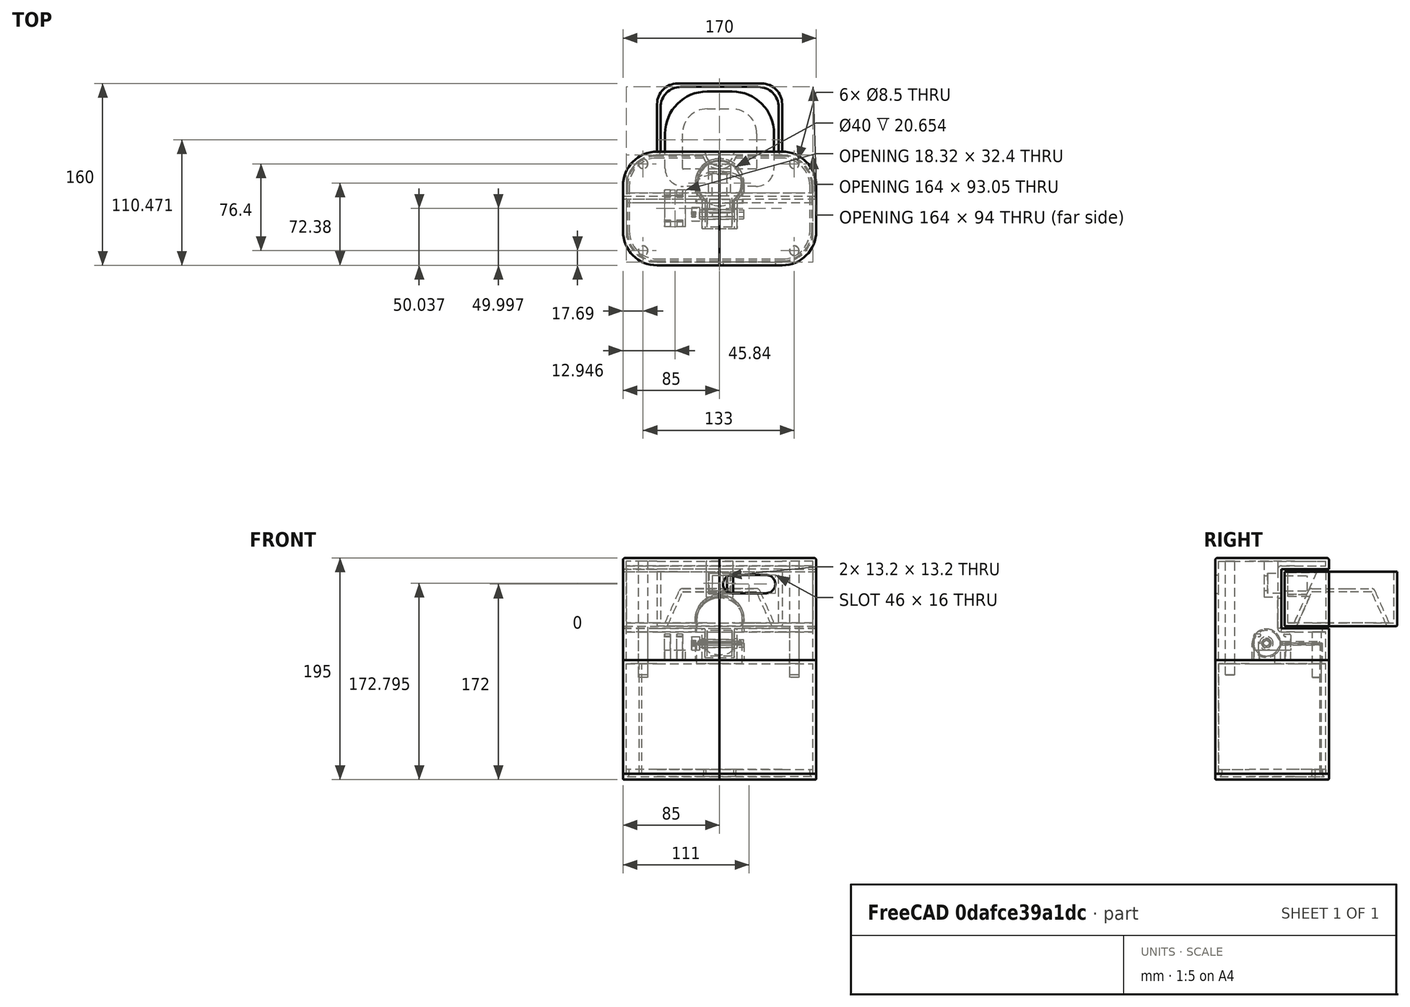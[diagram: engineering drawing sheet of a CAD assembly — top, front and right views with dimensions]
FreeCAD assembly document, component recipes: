
FREECAD ASSEMBLY — COMPONENT RECIPES ("Feeder V3")

This assembly document has 6 components, labeled P0..P5 below (a component is one placed body or linked part). 6 of them carry a construction recipe — the FreeCAD feature program that regenerates the part from scratch, quoted from this document or its linked companion documents; the rest are supplied as boundary geometry only. No exploded tour is included for this assembly.
COMPONENT P0 — recipe-attached ("Body001_CutLink", modeled in this document).
Construction recipe (the document's own serialized feature program — sketch geometry with constraints, then the solid features built on it; lengths are millimeters unless a unit is written):

FEATURE [PartDesign::Plane] CopyDatumPlane
  Length = 62.6838
  Placement = pos=(-2.6041e-12,-27.4425,215) rot=(0.707107,0.707107,0;3.14159rad)
  ResizeMode = 0
  Width = 60.2413
FEATURE [PartDesign::SubShapeBinder] Binder
  BindCopyOnChange = 0
  BindMode = 0
  ClaimChildren = false
  Context = -> Body001 [Binder.]
  Fuse = false
  MakeFace = true
  OffsetFill = false
  OffsetIntersection = false
  OffsetJoinType = 0
  OffsetOpenResult = false
  PartialLoad = false
  Refine = true
  Relative = true
  Support = -> [Body[Pocket004.Edge74,Pocket004.Face29,Pocket004.Face33,Pocket004.Edge73]]
  _Version = 2
FEATURE [Sketcher::SketchObject] Sketch011
  ArcFitTolerance = 1e-06
  AttachmentSupport = -> [Binder]
  ExternalGeometry = -> [Binder]
  FullyConstrained = true
  MakeInternals = false
  MapMode = 5
  Placement = pos=(-13,0,0) rot=(0.57735,0.57735,0.57735;2.0944rad)
  sketch-geometry (7):
    g0: LineSegment StartX=-31.6637 StartY=215 StartZ=0 EndX=-29.5387 EndY=211.319 EndZ=0
    g1: LineSegment StartX=-29.5387 StartY=211.319 StartZ=0 EndX=-25.2887 EndY=211.319 EndZ=0
    g2: LineSegment StartX=-25.2887 StartY=211.319 StartZ=0 EndX=-23.1637 EndY=215 EndZ=0
    g3: LineSegment StartX=-23.1637 StartY=215 StartZ=0 EndX=-25.2887 EndY=218.681 EndZ=0
    g4: LineSegment StartX=-25.2887 StartY=218.681 StartZ=0 EndX=-29.5387 EndY=218.681 EndZ=0
    g5: LineSegment StartX=-29.5387 StartY=218.681 StartZ=0 EndX=-31.6637 EndY=215 EndZ=0
    g6: Circle [constr] CenterX=-27.4137 CenterY=215 CenterZ=0 NormalX=0 NormalY=0 NormalZ=1 AngleXU=0 Radius=4.25
  constraints (19):
    c: Coincident(g0,g1)
    c: Coincident(g1,g2)
    c: Coincident(g2,g3)
    c: Coincident(g3,g4)
    c: Coincident(g4,g5)
    c: Coincident(g5,g0)
    c: Equal(g0, g1-g5) x5
    c: PointOnObject(g0,g6)
    c: PointOnObject(g1,g6)
    c: PointOnObject(g2,g6)
    c: PointOnObject(g3,g6)
    c: PointOnObject(g4,g6)
    c: PointOnObject(g5,g6)
    c: Coincident(g6,g-5)
    c: PointOnObject(g5,g-4)
    c: Horizontal(g2,g6)
    c: DistanceX(g-5,g-6) = 59.9137
    c: DistanceX(g-6,g-6) = 34.9137
    c: DistanceX(g-5,g-6) = 25
FEATURE [Sketcher::SketchObject] Sketch012
  ArcFitTolerance = 1e-06
  AttachmentSupport = -> [YZ_Plane001]
  ExternalGeometry = -> [Binder]
  FullyConstrained = true
  MakeInternals = false
  MapMode = 5
  Placement = pos=(0,0,0) rot=(0.57735,0.57735,0.57735;2.0944rad)
  sketch-geometry (7):
    g0: ArcOfCircle CenterX=-27.4137 CenterY=215 CenterZ=0 NormalX=0 NormalY=0 NormalZ=1 AngleXU=0 Radius=11.25 StartAngle=3.14159 EndAngle=5.83678
    g1: LineSegment StartX=-15.66 StartY=213.499 StartZ=0 EndX=-17.2662 EndY=210.143 EndZ=0
    g2: ArcOfCircle CenterX=-27.4137 CenterY=215 CenterZ=0 NormalX=0 NormalY=0 NormalZ=1 AngleXU=0 Radius=11.25 StartAngle=0.444057 EndAngle=3.14159
    g3: LineSegment StartX=-15.6685 StartY=216.499 StartZ=0 EndX=-17.2548 EndY=219.833 EndZ=0
    g4: LineSegment StartX=-15.6685 StartY=216.499 StartZ=0 EndX=0 EndY=216.499 EndZ=0
    g5: LineSegment StartX=0 StartY=216.499 StartZ=0 EndX=0 EndY=213.499 EndZ=0
    g6: LineSegment StartX=-15.66 StartY=213.499 StartZ=0 EndX=0 EndY=213.499 EndZ=0
  constraints (18):
    c: Horizontal(g0,g0)
    c: Tangent(g0,g1) = 1.5708
    c: Coincident(g0,g-4)
    c: Tangent(g2,g3) = -1.5708
    c: Radius(g2) = 11.25
    c: Horizontal(g4)
    c: Coincident(g3,g4)
    c: Coincident(g0,g2)
    c: DistanceY(g0,g2) = 9.69
    c: Coincident(g5,g4)
    c: Vertical(g5)
    c: Coincident(g0,g2)
    c: PointOnObject(g4,g-2)
    c: Block(g5)
    c: DistanceX(g1,g5) = 15.66
    c: Coincident(g6,g1)
    c: Coincident(g6,g5)
    c: Horizontal(g6)
FEATURE [PartDesign::Pad] Pad019  label="Door Pin width"
  Direction = (1,0,0)
  Length = 22
  Length2 = 10
  Midplane = true
  Placement = pos=(0,0,0) rot=(1,1,1;2.0944rad)
  Profile = -> Sketch012
  ReferenceAxis = -> Sketch012 [N_Axis]
  Refine = true
  Suppressed = false
  Type = 0
FEATURE [Sketcher::SketchObject] Sketch015
  ArcFitTolerance = 1e-06
  AttachmentSupport = -> [Pad019]
  FullyConstrained = true
  MakeInternals = false
  MapMode = 5
  Placement = pos=(0,4.76e-14,216.499) rot=(0,0,-1;1.5708rad)
  sketch-geometry (5):
    g0: LineSegment StartX=1.545e-13 StartY=-11 StartZ=0 EndX=1.616e-13 EndY=11 EndZ=0
    g1: LineSegment StartX=1.616e-13 StartY=11 StartZ=0 EndX=15.6637 EndY=11 EndZ=0
    g2: LineSegment StartX=1.545e-13 StartY=-11 StartZ=0 EndX=15.6637 EndY=-11 EndZ=0
    g3: LineSegment StartX=15.6637 StartY=11 StartZ=0 EndX=0 EndY=1.8e-15 EndZ=0
    g4: LineSegment StartX=0 StartY=1.8e-15 StartZ=0 EndX=15.6637 EndY=-11 EndZ=0
  constraints (10):
    c: Coincident(g0,g-4)
    c: Coincident(g0,g-6)
    c: Coincident(g1,g0)
    c: Coincident(g1,g-6)
    c: Coincident(g2,g0)
    c: Coincident(g2,g-5)
    c: Coincident(g3,g-6)
    c: Coincident(g3,g-1)
    c: Coincident(g4,g3)
    c: Coincident(g4,g2)
FEATURE [PartDesign::Pocket] Pocket014  label="Door Cut"
  BaseFeature = -> Pad019
  Direction = (0,0,-1)
  Length = 0
  Length2 = 5
  Placement = pos=(0,0,0) rot=(1,1,1;2.0944rad)
  Profile = -> Sketch015
  ReferenceAxis = -> Sketch015 [N_Axis]
  Refine = true
  Suppressed = false
  Type = 3
  UpToFace = -> Pad019 [Face2]
FEATURE [PartDesign::Pocket] Pocket015  label="Door Pin Hole"
  BaseFeature = -> Pocket014
  Direction = (-1,0,0)
  Length = 5
  Length2 = 5
  Placement = pos=(0,0,0) rot=(1,1,1;2.0944rad)
  Profile = -> Sketch011
  ReferenceAxis = -> Sketch011 [N_Axis]
  Refine = true
  Reversed = true
  Suppressed = false
  Type = 1
FEATURE [PartDesign::Revolution] Revolution
  Angle = 360
  Angle2 = 60
  Axis = (7e-16,-2e-16,-1)
  Base = (-1.665e-13,1.202e-13,216.499)
  BaseFeature = -> Pocket015
  Placement = pos=(0,0,0) rot=(1,1,1;2.0944rad)
  Profile = -> Pocket015 [Face8]
  ReferenceAxis = -> Pocket015 [Edge37]
  Refine = true
  Suppressed = false
  Type = 3
  UpToFace = -> Pocket015 [Face9]
FEATURE [PartDesign::Fillet] Fillet001
  Base = -> Revolution [Edge32,Edge1]
  BaseFeature = -> Revolution
  Placement = pos=(0,0,0) rot=(1,1,1;2.0944rad)
  Radius = 4
  Refine = true
  SupportTransform = false
  Suppressed = false
  UseAllEdges = false
FEATURE [PartDesign::Body] Body001  label="Storage Door"
  AllowCompound = false
  Group = -> [CopyDatumPlane,Binder,Sketch011,Sketch012,Sketch015,Pad019,Pocket014,Pocket015,Revolution,Fillet001]
  Origin = -> Origin001
  Tip = -> Fillet001
COMPONENT P1 — recipe-attached ("Body002_CutLink", modeled in this document).
Construction recipe (the document's own serialized feature program — sketch geometry with constraints, then the solid features built on it; lengths are millimeters unless a unit is written):

FEATURE [PartDesign::SubShapeBinder] Binder001
  BindCopyOnChange = 0
  BindMode = 0
  ClaimChildren = false
  Context = -> Body002 [Binder001.]
  Fuse = false
  MakeFace = true
  OffsetFill = false
  OffsetIntersection = false
  OffsetJoinType = 0
  OffsetOpenResult = false
  PartialLoad = false
  Refine = true
  Relative = true
  Support = -> [Body[Pocket004.Face23,Pocket004.Face21]]
  _Version = 2
FEATURE [PartDesign::SubShapeBinder] Binder002
  BindCopyOnChange = 0
  BindMode = 0
  ClaimChildren = false
  Context = -> Body002 [Binder002.]
  Fuse = false
  MakeFace = true
  OffsetFill = false
  OffsetIntersection = false
  OffsetJoinType = 0
  OffsetOpenResult = false
  PartialLoad = false
  Refine = true
  Relative = true
  Support = -> [Body001[Pocket006.Face3]]
  _Version = 2
FEATURE [PartDesign::Plane] CopyDatumPlane001
  Length = 74.8801
  Placement = pos=(0,-27.4425,215) rot=(0.57735,0.57735,0.57735;2.0944rad)
  ResizeMode = 0
  Width = 262.438
FEATURE [Sketcher::SketchObject] Sketch016
  ArcFitTolerance = 1e-06
  AttachmentSupport = -> [CopyDatumPlane001]
  ExternalGeometry = -> [Binder002]
  FullyConstrained = true
  MakeInternals = false
  MapMode = 5
  Placement = pos=(0,-27.4425,215) rot=(0.57735,0.57735,0.57735;2.0944rad)
  sketch-geometry (7):
    g0: LineSegment StartX=3.9 StartY=0 StartZ=0 EndX=1.95 EndY=3.3775 EndZ=0
    g1: LineSegment StartX=1.95 StartY=3.3775 StartZ=0 EndX=-1.95 EndY=3.3775 EndZ=0
    g2: LineSegment StartX=-1.95 StartY=3.3775 StartZ=0 EndX=-3.9 EndY=4.765e-13 EndZ=0
    g3: LineSegment StartX=-3.9 StartY=4.765e-13 StartZ=0 EndX=-1.95 EndY=-3.3775 EndZ=0
    g4: LineSegment StartX=-1.95 StartY=-3.3775 StartZ=0 EndX=1.95 EndY=-3.3775 EndZ=0
    g5: LineSegment StartX=1.95 StartY=-3.3775 StartZ=0 EndX=3.9 EndY=0 EndZ=0
    g6: Circle [constr] CenterX=0 CenterY=0 CenterZ=0 NormalX=0 NormalY=0 NormalZ=1 AngleXU=0 Radius=3.9
  constraints (16):
    c: Coincident(g0,g1)
    c: Coincident(g1,g2)
    c: Coincident(g2,g3)
    c: Coincident(g3,g4)
    c: Coincident(g4,g5)
    c: Coincident(g5,g0)
    c: Equal(g0, g1-g5) x5
    c: PointOnObject(g0,g6)
    c: PointOnObject(g1,g6)
    c: PointOnObject(g2,g6)
    c: PointOnObject(g3,g6)
    c: PointOnObject(g4,g6)
    c: PointOnObject(g5,g6)
    c: Radius(g6) = 3.9
    c: Coincident(g6,g-1)
    c: PointOnObject(g5,g-1)
FEATURE [PartDesign::Pad] Pad005  label="Square Push"
  Direction = (1,0,0)
  Length = 42
  Length2 = 10
  Midplane = true
  Placement = pos=(0,-27.4425,215) rot=(0.57735,0.57735,0.57735;2.0944rad)
  Profile = -> Sketch016
  ReferenceAxis = -> Sketch016 [N_Axis]
  Refine = true
  Suppressed = false
  Type = 0
FEATURE [Sketcher::SketchObject] Sketch017
  ArcFitTolerance = 1e-06
  AttachmentSupport = -> [Pad005]
  FullyConstrained = true
  MakeInternals = false
  MapMode = 5
  Placement = pos=(-21,-27.4425,215) rot=(0.57735,0.57735,-0.57735;4.18879rad)
  sketch-geometry (1):
    g0: Circle CenterX=0 CenterY=0 CenterZ=0 NormalX=0 NormalY=0 NormalZ=1 AngleXU=0 Radius=5.9
  constraints (2):
    c: Diameter(g0) = 11.8
    c: Coincident(g0,g-1)
FEATURE [PartDesign::Pad] Pad006  label="Circle push"
  BaseFeature = -> Pad005
  Direction = (-1,0,0)
  Length = 7
  Length2 = 10
  Midplane = true
  Placement = pos=(0,-27.4425,215) rot=(0.57735,0.57735,0.57735;2.0944rad)
  Profile = -> Sketch017
  ReferenceAxis = -> Sketch017 [N_Axis]
  Refine = true
  Suppressed = false
  Type = 0
FEATURE [PartDesign::SubShapeBinder] Binder003  label="Axle Binder"
  BindCopyOnChange = 0
  BindMode = 0
  ClaimChildren = false
  Context = -> Body002 [Binder003.]
  Fuse = false
  MakeFace = true
  OffsetFill = false
  OffsetIntersection = false
  OffsetJoinType = 0
  OffsetOpenResult = false
  PartialLoad = false
  Placement = pos=(3.5,-1.07e-14,0) rot=(0,0,1;0rad)
  Refine = true
  Relative = true
  _Version = 2
FEATURE [Sketcher::SketchObject] Sketch018
  ArcFitTolerance = 1e-06
  AttachmentSupport = -> [Pad006]
  ExternalGeometry = -> [Binder003]
  FullyConstrained = true
  MakeInternals = false
  MapMode = 5
  Placement = pos=(-24.5,-27.4425,215) rot=(0.57735,0.57735,-0.57735;4.18879rad)
  sketch-geometry (5):
    g0: LineSegment StartX=0 StartY=0 StartZ=0 EndX=0 EndY=2.375 EndZ=0
    g1: LineSegment StartX=0 StartY=2.375 StartZ=0 EndX=-0.0980568 EndY=2.47306 EndZ=0
    g2: LineSegment StartX=-0.0980568 StartY=2.47306 StartZ=0 EndX=-0.160985 EndY=2.46976 EndZ=0
    g3: LineSegment StartX=-0.160985 StartY=2.46976 StartZ=0 EndX=-0.248255 EndY=2.36199 EndZ=0
    g4: LineSegment StartX=-0.248255 StartY=2.36199 StartZ=0 EndX=0 EndY=0 EndZ=0
  constraints (10):
    c: Coincident(g0,g-1)
    c: Coincident(g0,g-4)
    c: Coincident(g1,g0)
    c: Coincident(g1,g-4)
    c: Coincident(g3,g2)
    c: Coincident(g3,g-5)
    c: Coincident(g4,g3)
    c: Coincident(g4,g0)
    c: Coincident(g2,g-5)
    c: Coincident(g2,g1)
FEATURE [PartDesign::Pocket] Pocket007  label="Axle form"
  BaseFeature = -> Pad006
  Direction = (1,0,0)
  Length = 3.5
  Length2 = 5
  Placement = pos=(0,-27.4425,215) rot=(0.57735,0.57735,0.57735;2.0944rad)
  Profile = -> Sketch018
  ReferenceAxis = -> Sketch018 [N_Axis]
  Refine = true
  Suppressed = false
  Type = 0
FEATURE [PartDesign::PolarPattern] PolarPattern  label="Axle repeat round"
  Angle = 360
  Axis = -> Sketch018 [N_Axis]
  BaseFeature = -> Pocket007
  Mode = 0
  Occurrences = 60
  Offset = 120
  Originals = -> [Pocket007]
  Placement = pos=(0,-27.4425,215) rot=(0.57735,0.57735,0.57735;2.0944rad)
  Refine = true
  Suppressed = false
  TransformMode = 0
FEATURE [PartDesign::Body] Body002  label="Storage Door Pin"
  AllowCompound = false
  Group = -> [Binder001,Binder002,CopyDatumPlane001,Sketch016,Pad005,Sketch017,Pad006,Sketch018,Binder003,Pocket007,PolarPattern]
  Origin = -> Origin002
  Tip = -> PolarPattern
COMPONENT P2 — recipe-attached ("Body006_CutLink", modeled in this document).
Construction recipe (the document's own serialized feature program — sketch geometry with constraints, then the solid features built on it; lengths are millimeters unless a unit is written):

FEATURE [PartDesign::ShapeBinder] ShapeBinder001  label="Base Shape Binder"
  Support = -> [Pocket008]
  TraceSupport = false
FEATURE [PartDesign::Pad] Pad015  label="Height of base"
  Direction = (0,0,1)
  Length = 90
  Length2 = 10
  Profile = -> ShapeBinder001
  Refine = true
  Suppressed = false
  Type = 0
FEATURE [PartDesign::ShapeBinder] CopyPocket009  label="Storage Door Datum"
  Placement = pos=(0,0,215) rot=(0,0,1;0rad)
  TraceSupport = false
FEATURE [PartDesign::Line] DatumLine001  label="Storage Door Center"
  AttacherType = Attacher::AttachEngineLine
  AttachmentSupport = -> [CopyPocket009]
  Length = 20
  MapMode = 19
  Placement = pos=(0,0,215) rot=(0,0,-1;0.736025rad)
  ResizeMode = 0
FEATURE [PartDesign::Point] DatumPoint001  label="Storage Door Axle"
  AttacherType = Attacher::AttachEnginePoint
  AttachmentSupport = -> [Pocket008]
  MapMode = 36
  Placement = pos=(-15.5,-27.4137,215) rot=(0.707107,0.707107,0;3.14159rad)
FEATURE [Sketcher::SketchObject] Sketch034
  ArcFitTolerance = 1e-06
  AttachmentSupport = -> [Pad015]
  ExternalGeometry = -> [DatumPoint001,CopyPocket009,Pad015]
  FullyConstrained = true
  MakeInternals = false
  MapMode = 5
  Placement = pos=(85,0,0) rot=(0.57735,0.57735,0.57735;2.0944rad)
  sketch-geometry (4):
    g0: LineSegment StartX=84.996 StartY=228 StartZ=0 EndX=84.996 EndY=280 EndZ=0
    g1: LineSegment StartX=84.996 StartY=280 StartZ=0 EndX=-14.434 EndY=280 EndZ=0
    g2: LineSegment StartX=-14.434 StartY=280 StartZ=0 EndX=-14.434 EndY=228 EndZ=0
    g3: LineSegment StartX=-14.434 StartY=228 StartZ=0 EndX=84.996 EndY=228 EndZ=0
  constraints (12):
    c: Coincident(g0,g1)
    c: Coincident(g1,g2)
    c: Coincident(g2,g3)
    c: Coincident(g3,g0)
    c: Vertical(g0)
    c: Vertical(g2)
    c: Horizontal(g1)
    c: Horizontal(g3)
    c: DistanceY(g2,g2) = 52
    c: PointOnObject(g-4,g2)
    c: Distance(g-6,g1) = 10
    c: DistanceX(g3,g3) = 99.43
FEATURE [PartDesign::ShapeBinder] CopyPocket010  label="Hinge length"
  Placement = pos=(0,0,215) rot=(0,0,1;0rad)
  TraceSupport = false
FEATURE [PartDesign::Pocket] Pocket009  label="Food Plate Cut"
  BaseFeature = -> Pad015
  Direction = (-1,0,0)
  Length = 0
  Length2 = 5
  Profile = -> Sketch034
  ReferenceAxis = -> Sketch034 [N_Axis]
  Refine = true
  Suppressed = false
  Type = 3
  UpToFace = -> Pad015 [Face3]
FEATURE [PartDesign::Thickness] Thickness001
  Base = -> Pocket009 [Face2]
  BaseFeature = -> Pocket009
  Intersection = false
  Join = 0
  Mode = 0
  Refine = true
  Reversed = true
  SupportTransform = false
  Suppressed = false
  Value = 3
FEATURE [Sketcher::SketchObject] Sketch037
  ArcFitTolerance = 1e-06
  AttachmentSupport = -> [Thickness001]
  ExternalGeometry = -> [CopyPocket009]
  FullyConstrained = true
  MakeInternals = false
  MapMode = 5
  Placement = pos=(0,0,225) rot=(1,0,0;3.14159rad)
  sketch-geometry (6):
    g0: ArcOfCircle CenterX=0 CenterY=0 CenterZ=0 NormalX=0 NormalY=0 NormalZ=1 AngleXU=0 Radius=21.5 StartAngle=3.0286 EndAngle=6.39618
    g1: LineSegment StartX=20 StartY=34.4342 StartZ=0 EndX=20 EndY=14.4342 EndZ=0
    g2: LineSegment StartX=-20 StartY=34.4342 StartZ=0 EndX=-20 EndY=14.4342 EndZ=0
    g3: ArcOfCircle CenterX=3.5332e-12 CenterY=-35.523 CenterZ=0 NormalX=0 NormalY=0 NormalZ=1 AngleXU=0 Radius=72.76 StartAngle=1.29234 EndAngle=1.84926
    g4: LineSegment StartX=20 StartY=14.4342 StartZ=0 EndX=21.3629 EndY=2.42425 EndZ=0
    g5: LineSegment StartX=-20 StartY=14.4342 StartZ=0 EndX=-21.3629 EndY=2.42425 EndZ=0
  constraints (19):
    c: Coincident(g0,g-1)
    c: Coincident(g3,g2)
    c: Coincident(g1,g3)
    c: DistanceX(g-6,g2) = 3
    c: DistanceX(g1,g-5) = 3
    c: Vertical(g2,g2)
    c: Horizontal(g2,g1)
    c: Radius(g3) = 72.76
    c: Tangent(g0,g5) = -1.5708
    c: Radius(g0) = 21.5
    c: Coincident(g5,g2)
    c: Tangent(g0,g4) = 1.5708
    c: Coincident(g1,g4)
    c: Horizontal(g1,g2)
    c: Vertical(g1)
    c: DistanceY(g5,g5) = 12.01
    c: DistanceY(g4,g4) = 12.01
    c: DistanceY(g1,g1) = 20
    c: DistanceY(g-5,g-5) = 23
FEATURE [PartDesign::Pocket] Pocket010  label="Food door cut"
  BaseFeature = -> Thickness001
  Direction = (0,0,1)
  Length = 0
  Length2 = 5
  Profile = -> Sketch037
  ReferenceAxis = -> Sketch037 [N_Axis]
  Refine = true
  Suppressed = false
  Type = 3
  UpToFace = -> Thickness001 [Face3]
FEATURE [Sketcher::SketchObject] Sketch054
  ArcFitTolerance = 1e-06
  AttachmentSupport = -> [Pocket010]
  ExternalGeometry = -> [Pocket010]
  FullyConstrained = true
  MakeInternals = false
  MapMode = 5
  Placement = pos=(0,-14.434,0) rot=(0,0.707107,0.707107;3.14159rad)
  sketch-geometry (1):
    g0: Circle CenterX=-3.5467e-12 CenterY=233.933 CenterZ=0 NormalX=0 NormalY=0 NormalZ=1 AngleXU=0 Radius=20.8615
  constraints (3):
    c: PointOnObject(g-3,g0)
    c: PointOnObject(g-3,g0)
    c: Block(g0)
FEATURE [PartDesign::Pocket] Pocket024  label="Food door cut001"
  BaseFeature = -> Pocket010
  Direction = (0,-1,2e-16)
  Length = 0
  Length2 = 5
  Profile = -> Sketch054
  ReferenceAxis = -> Sketch054 [N_Axis]
  Refine = true
  Suppressed = false
  Type = 3
  UpToFace = -> Pocket010 [Face32]
FEATURE [Sketcher::SketchObject] Sketch056  label="HX711 Hole"
  ArcFitTolerance = 1e-06
  AttachmentSupport = -> [Pocket024]
  ExternalGeometry = -> [DatumLine001,Pocket024]
  FullyConstrained = true
  MakeInternals = false
  MapMode = 5
  Placement = pos=(0,-14.434,0) rot=(0,0.707107,0.707107;3.14159rad)
  sketch-geometry (10):
    g0: LineSegment StartX=-9 StartY=276.795 StartZ=0 EndX=-9 EndY=258.795 EndZ=0
    g1: LineSegment StartX=-9 StartY=258.795 StartZ=0 EndX=9 EndY=258.795 EndZ=0
    g2: LineSegment StartX=9 StartY=258.795 StartZ=0 EndX=9 EndY=276.795 EndZ=0
    g3: LineSegment StartX=9 StartY=276.795 StartZ=0 EndX=-9 EndY=276.795 EndZ=0
    g4: GeomPoint [constr] X=2.1e-15 Y=267.795 Z=0
    g5: LineSegment StartX=6.6 StartY=261.195 StartZ=0 EndX=6.6 EndY=274.395 EndZ=0
    g6: LineSegment StartX=6.6 StartY=274.395 StartZ=0 EndX=-6.6 EndY=274.395 EndZ=0
    g7: LineSegment StartX=-6.6 StartY=274.395 StartZ=0 EndX=-6.6 EndY=261.195 EndZ=0
    g8: LineSegment StartX=-6.6 StartY=261.195 StartZ=0 EndX=6.6 EndY=261.195 EndZ=0
    g9: GeomPoint [constr] X=2.1e-15 Y=267.795 Z=0
  constraints (25):
    c: Coincident(g0,g1)
    c: Coincident(g1,g2)
    c: Coincident(g2,g3)
    c: Coincident(g3,g0)
    c: Vertical(g0)
    c: Vertical(g2)
    c: Horizontal(g1)
    c: Horizontal(g3)
    c: Symmetric(g2,g0,g4)
    c: PointOnObject(g4,g-3)
    c: DistanceX(g3,g3) = 18
    c: DistanceY(g0,g0) = 18
    c: Distance(g-4,g1) = 4
    c: Coincident(g5,g6)
    c: Coincident(g6,g7)
    c: Coincident(g7,g8)
    c: Coincident(g8,g5)
    c: Vertical(g5)
    c: Vertical(g7)
    c: Horizontal(g6)
    c: Horizontal(g8)
    c: Symmetric(g7,g5,g9)
    c: Coincident(g9,g4)
    c: DistanceX(g8,g8) = 13.2
    c: DistanceY(g7,g7) = 13.2
FEATURE [Sketcher::SketchObject] Sketch057
  ArcFitTolerance = 1e-06
  AttachmentSupport = -> [Pocket024]
  ExternalGeometry = -> [Sketch056,Pocket024]
  FullyConstrained = true
  MakeInternals = false
  MapMode = 5
  Placement = pos=(0,-17.434,0) rot=(1,0,0;1.5708rad)
  sketch-geometry (4):
    g0: LineSegment StartX=-12 StartY=290 StartZ=0 EndX=-12 EndY=255.795 EndZ=0
    g1: LineSegment StartX=-12 StartY=255.795 StartZ=0 EndX=12 EndY=255.795 EndZ=0
    g2: LineSegment StartX=12 StartY=255.795 StartZ=0 EndX=12 EndY=290 EndZ=0
    g3: LineSegment StartX=12 StartY=290 StartZ=0 EndX=-12 EndY=290 EndZ=0
  constraints (11):
    c: Coincident(g0,g1)
    c: Coincident(g1,g2)
    c: Coincident(g2,g3)
    c: Coincident(g3,g0)
    c: Vertical(g0)
    c: Vertical(g2)
    c: Horizontal(g1)
    c: PointOnObject(g0,g-4)
    c: Distance(g1,g-5) = 3
    c: Symmetric(g0,g2,g-2)
    c: Distance(g0,g-6) = 3
FEATURE [PartDesign::Pad] Pad026  label="HX71 Hole width"
  BaseFeature = -> Pocket024
  Direction = (0,-1,2e-16)
  Length = 12
  Length2 = 10
  Profile = -> Sketch057
  ReferenceAxis = -> Sketch057 [N_Axis]
  Refine = true
  Suppressed = false
  Type = 0
FEATURE [PartDesign::Pocket] Pocket027
  BaseFeature = -> Pad026
  Direction = (0,-1,2e-16)
  Length = 0
  Length2 = 5
  Profile = -> Sketch056 [Edge7,Edge8,Edge5,Edge6]
  ReferenceAxis = -> Sketch056 [N_Axis]
  Refine = true
  Suppressed = false
  Type = 3
  UpToFace = -> Pad026 [Face40]
FEATURE [Sketcher::SketchObject] Sketch060
  ArcFitTolerance = 1e-06
  AttachmentSupport = -> [Pocket027]
  ExternalGeometry = -> [Pocket027]
  FullyConstrained = true
  MakeInternals = false
  MapMode = 5
  Placement = pos=(0,-72.3831,0) rot=(1,0,0;1.5708rad)
  sketch-geometry (4):
    g0: ArcOfCircle CenterX=41 CenterY=267 CenterZ=0 NormalX=0 NormalY=0 NormalZ=1 AngleXU=0 Radius=8 StartAngle=4.71239 EndAngle=7.85398
    g1: ArcOfCircle CenterX=11 CenterY=267 CenterZ=0 NormalX=0 NormalY=0 NormalZ=1 AngleXU=0 Radius=8 StartAngle=1.5708 EndAngle=4.71239
    g2: LineSegment StartX=41 StartY=259 StartZ=0 EndX=11 EndY=259 EndZ=0
    g3: LineSegment StartX=41 StartY=275 StartZ=0 EndX=11 EndY=275 EndZ=0
  constraints (10):
    c: Tangent(g0,g2) = 1.5708
    c: Tangent(g0,g3) = -1.5708
    c: Tangent(g1,g2) = 1.5708
    c: Tangent(g1,g3) = -1.5708
    c: Equal(g0,g1)
    c: Horizontal(g3)
    c: Distance(g0,g1) = 30
    c: Radius(g0) = 8
    c: Distance(g-3,g3) = 15
    c: Distance(g0,g-5) = 6
FEATURE [PartDesign::Pocket] Pocket030
  BaseFeature = -> Pocket027
  Direction = (0,1,-2e-16)
  Length = 0
  Length2 = 5
  Profile = -> Sketch060
  ReferenceAxis = -> Sketch060 [N_Axis]
  Refine = true
  Suppressed = false
  Type = 3
  UpToFace = -> Pocket027 [Face15]
FEATURE [PartDesign::Fillet] Fillet004
  Base = -> Pocket030 [Face23]
  BaseFeature = -> Pocket030
  Radius = 2
  Refine = true
  SupportTransform = false
  Suppressed = false
  UseAllEdges = false
FEATURE [PartDesign::ShapeBinder] ShapeBinder004  label="Screw Holes"
  Support = -> [Fillet008]
  TraceSupport = false
FEATURE [Sketcher::SketchObject] Sketch063
  ArcFitTolerance = 1e-06
  AttachmentSupport = -> [Fillet004]
  ExternalGeometry = -> [ShapeBinder004]
  FullyConstrained = true
  MakeInternals = false
  MapMode = 5
  Placement = pos=(0,0,287) rot=(1,0,0;3.14159rad)
  sketch-geometry (2):
    g0: Circle CenterX=-67.31 CenterY=59.4338 CenterZ=0 NormalX=0 NormalY=0 NormalZ=1 AngleXU=0 Radius=4.05
    g1: Circle CenterX=65.69 CenterY=59.4338 CenterZ=0 NormalX=0 NormalY=0 NormalZ=1 AngleXU=0 Radius=4.05
  constraints (4):
    c: Diameter(g0) = 8.1
    c: Coincident(g0,g-4)
    c: Diameter(g1) = 8.1
    c: Coincident(g1,g-5)
FEATURE [Sketcher::SketchObject] Sketch064
  ArcFitTolerance = 1e-06
  AttachmentSupport = -> [Fillet004]
  ExternalGeometry = -> [ShapeBinder004]
  FullyConstrained = true
  MakeInternals = false
  MapMode = 5
  Placement = pos=(0,0,225) rot=(1,0,0;3.14159rad)
  sketch-geometry (2):
    g0: Circle CenterX=-67.31 CenterY=-16.9662 CenterZ=0 NormalX=0 NormalY=0 NormalZ=1 AngleXU=0 Radius=4.05
    g1: Circle CenterX=65.69 CenterY=-16.9662 CenterZ=0 NormalX=0 NormalY=0 NormalZ=1 AngleXU=0 Radius=4.05
  constraints (4):
    c: Coincident(g0,g-4)
    c: Distance(g0,g-4) = 0.2
    c: Coincident(g1,g-3)
    c: Distance(g1,g-3) = 0.2
FEATURE [PartDesign::Pad] Pad030
  BaseFeature = -> Fillet004
  Direction = (0,0,-1)
  Length = 40
  Length2 = 10
  Profile = -> Sketch064
  ReferenceAxis = -> Sketch064 [N_Axis]
  Refine = true
  Suppressed = false
  Type = 0
FEATURE [PartDesign::Pad] Pad031
  BaseFeature = -> Pad030
  Direction = (0,0,-1)
  Length = 100
  Length2 = 10
  Profile = -> Sketch063
  ReferenceAxis = -> Sketch063 [N_Axis]
  Refine = true
  Suppressed = false
  Type = 0
FEATURE [PartDesign::Pocket] Pocket034
  BaseFeature = -> Pad031
  Direction = (0,-1,2e-16)
  Length = 12
  Length2 = 5
  Profile = -> Sketch056 [Edge3,Edge2,Edge1,Edge4]
  ReferenceAxis = -> Sketch056 [N_Axis]
  Refine = true
  Suppressed = false
  Type = 0
FEATURE [PartDesign::Body] Body006  label="Food Base"
  AllowCompound = false
  Group = -> [CopyPocket009,DatumLine001,ShapeBinder001,DatumPoint001,CopyPocket010,Pad015,Sketch034,Pocket009,Thickness001,Sketch037,Pocket010,Sketch054,Pocket024,Sketch056,Sketch057,Pad026,Pocket027,Sketch060,Pocket030,Fillet004,ShapeBinder004,Sketch063,Sketch064,Pad030,Pad031,Pocket034]
  Origin = -> Origin006
  Tip = -> Pocket034
COMPONENT P3 — recipe-attached ("Body009_CutLink", modeled in this document).
Construction recipe (the document's own serialized feature program — sketch geometry with constraints, then the solid features built on it; lengths are millimeters unless a unit is written):

FEATURE [PartDesign::ShapeBinder] CopyPocket017  label="Food base form"
  Support = -> [Pocket024]
  TraceSupport = false
FEATURE [Sketcher::SketchObject] Sketch048
  ArcFitTolerance = 1e-06
  AttachmentSupport = -> [CopyPocket017]
  ExternalGeometry = -> [CopyPocket017]
  FullyConstrained = true
  MakeInternals = false
  MapMode = 5
  Placement = pos=(0,0,280) rot=(1,0,0;3.14159rad)
  sketch-geometry (8):
    g0: ArcOfCircle CenterX=-55 CenterY=2.38314 CenterZ=0 NormalX=0 NormalY=0 NormalZ=1 AngleXU=1.5708 Radius=30 StartAngle=1.5708 EndAngle=3.14159
    g1: LineSegment StartX=-55 StartY=-27.6169 StartZ=0 EndX=-55 EndY=-87.6169 EndZ=0
    g2: LineSegment StartX=-55 StartY=-87.6169 StartZ=0 EndX=55 EndY=-87.6169 EndZ=0
    g3: ArcOfCircle CenterX=55 CenterY=2.38314 CenterZ=0 NormalX=0 NormalY=0 NormalZ=1 AngleXU=1.5708 Radius=30 StartAngle=3.14159 EndAngle=4.71239
    g4: LineSegment StartX=55 StartY=-27.6169 StartZ=0 EndX=55 EndY=-87.6169 EndZ=0
    g5: LineSegment StartX=-85 StartY=2.38314 StartZ=0 EndX=-85 EndY=11.434 EndZ=0
    g6: LineSegment StartX=-85 StartY=11.434 StartZ=0 EndX=85 EndY=11.434 EndZ=0
    g7: LineSegment StartX=85 StartY=2.38314 StartZ=0 EndX=85 EndY=11.434 EndZ=0
  constraints (22):
    c: Coincident(g0,g-5)
    c: Coincident(g1,g2)
    c: Vertical(g1)
    c: Horizontal(g2)
    c: Distance(g2,g1) = 60
    c: Coincident(g1,g0)
    c: DistanceX(g2,g2) = 110
    c: Horizontal(g-5,g3)
    c: Vertical(g0,g-5)
    c: Coincident(g3,g-6)
    c: Block(g3)
    c: Coincident(g4,g3)
    c: Coincident(g4,g2)
    c: Coincident(g5,g0)
    c: PointOnObject(g5,g-3)
    c: Coincident(g6,g5)
    c: Horizontal(g6)
    c: Coincident(g7,g3)
    c: Coincident(g7,g6)
    c: Vertical(g7)
    c: Distance(g5,g-4) = 3
    c: Coincident(g0,g-5)
FEATURE [PartDesign::Pad] Pad024  label="Plate height"
  Direction = (0,0,-1)
  Length = 50
  Length2 = 10
  Profile = -> Sketch048
  ReferenceAxis = -> Sketch048 [N_Axis]
  Refine = true
  Suppressed = false
  Type = 0
FEATURE [Sketcher::SketchObject] Sketch050
  ArcFitTolerance = 1e-06
  AttachmentSupport = -> [Pad024]
  ExternalGeometry = -> [Pad024]
  FullyConstrained = true
  MakeInternals = false
  MapMode = 5
  Placement = pos=(0,0,230) rot=(1,0,0;3.14159rad)
  sketch-geometry (13):
    g0: LineSegment StartX=-46 StartY=-13.0173 StartZ=0 EndX=-46 EndY=-43.6291 EndZ=0
    g1: LineSegment StartX=-11.0122 StartY=-78.6169 StartZ=0 EndX=11.0122 EndY=-78.6169 EndZ=0
    g2: LineSegment StartX=46 StartY=-43.6291 StartZ=0 EndX=46 EndY=-13.0173 EndZ=0
    g3: LineSegment StartX=32.0488 StartY=0.933964 StartZ=0 EndX=-32.0488 EndY=0.933964 EndZ=0
    g4: GeomPoint [constr] X=0 Y=-38.8414 Z=0
    g5: ArcOfCircle CenterX=11.0122 CenterY=-43.6291 CenterZ=0 NormalX=0 NormalY=0 NormalZ=1 AngleXU=0 Radius=34.9878 StartAngle=4.71239 EndAngle=6.28319
    g6: GeomPoint [constr] X=46 Y=-78.6169 Z=0
    g7: ArcOfCircle CenterX=-11.0122 CenterY=-43.6291 CenterZ=0 NormalX=0 NormalY=0 NormalZ=1 AngleXU=0 Radius=34.9878 StartAngle=3.14159 EndAngle=4.71239
    g8: GeomPoint [constr] X=-46 Y=-78.6169 Z=0
    g9: ArcOfCircle CenterX=32.0488 CenterY=-13.0173 CenterZ=0 NormalX=0 NormalY=0 NormalZ=1 AngleXU=0 Radius=13.9512 StartAngle=-1.652e-13 EndAngle=1.5708
    g10: GeomPoint [constr] X=46 Y=0.933964 Z=0
    g11: ArcOfCircle CenterX=-32.0488 CenterY=-13.0173 CenterZ=0 NormalX=0 NormalY=0 NormalZ=1 AngleXU=0 Radius=13.9512 StartAngle=1.5708 EndAngle=3.14159
    g12: GeomPoint [constr] X=-46 Y=0.933964 Z=0
  constraints (29):
    c: Vertical(g0)
    c: Vertical(g2)
    c: Horizontal(g1)
    c: Horizontal(g3)
    c: Symmetric(g6,g12,g4)
    c: PointOnObject(g4,g-2)
    c: Distance(g-4,g2) = 9
    c: Distance(g10,g-3) = 12
    c: PointOnObject(g6,g1)
    c: PointOnObject(g6,g2)
    c: Tangent(g1,g5) = -1.5708
    c: Tangent(g2,g5) = -1.5708
    c: PointOnObject(g8,g0)
    c: PointOnObject(g8,g1)
    c: Tangent(g0,g7) = -1.5708
    c: Tangent(g1,g7) = -1.5708
    c: PointOnObject(g10,g2)
    c: PointOnObject(g10,g3)
    c: Tangent(g2,g9) = -1.5708
    c: Tangent(g3,g9) = -1.5708
    c: PointOnObject(g12,g0)
    c: PointOnObject(g12,g3)
    c: Tangent(g0,g11) = -1.5708
    c: Tangent(g3,g11) = -1.5708
    c: Distance(g-6,g1) = 9
    c: Horizontal(g7,g5)
    c: Block(g7)
    c: Horizontal(g11,g9)
    c: Block(g11)
FEATURE [PartDesign::Pocket] Pocket025  label="Plate Bowl cut"
  BaseFeature = -> Pad024
  Direction = (0,0,1)
  Length = 30
  Length2 = 5
  Profile = -> Sketch050
  ReferenceAxis = -> Sketch050 [N_Axis]
  Refine = true
  Suppressed = false
  TaperAngle = -24
  Type = 0
FEATURE [Sketcher::SketchObject] Sketch052
  ArcFitTolerance = 1e-06
  AttachmentSupport = -> [Pocket025]
  FullyConstrained = true
  MakeInternals = false
  MapMode = 5
  Placement = pos=(0,-11.434,0) rot=(1,0,0;1.5708rad)
  sketch-geometry (2):
    g0: ArcOfCircle CenterX=0 CenterY=236.136 CenterZ=0 NormalX=0 NormalY=0 NormalZ=1 AngleXU=0 Radius=21.5 StartAngle=5.99378 EndAngle=9.71418
    g1: LineSegment StartX=-20.6059 StartY=230 StartZ=0 EndX=20.6059 EndY=230 EndZ=0
  constraints (6):
    c: Coincident(g0,g-3)
    c: Diameter(g0) = 43
    c: PointOnObject(g1,g-4)
    c: Horizontal(g1)
    c: Coincident(g0,g1)
    c: Coincident(g0,g1)
FEATURE [PartDesign::Thickness] Thickness002
  Base = -> Pocket025 [Face4]
  BaseFeature = -> Pocket025
  Intersection = false
  Join = 0
  Mode = 0
  Refine = true
  Reversed = true
  SupportTransform = false
  Suppressed = false
  Value = 3
FEATURE [PartDesign::Pad] Pad025
  BaseFeature = -> Thickness002
  Direction = (0,-1,2e-16)
  Length = 10
  Length2 = 10
  Profile = -> Sketch052
  ReferenceAxis = -> Sketch052 [N_Axis]
  Refine = true
  Suppressed = false
  Type = 3
  UpToFace = -> Thickness002 [Face43]
FEATURE [Sketcher::SketchObject] Sketch055
  ArcFitTolerance = 1e-06
  AttachmentSupport = -> [Pad025]
  ExternalGeometry = -> [Sketch052]
  FullyConstrained = true
  MakeInternals = false
  MapMode = 5
  Placement = pos=(0,-11.434,0) rot=(1,0,0;1.5708rad)
  sketch-geometry (1):
    g0: Circle CenterX=0 CenterY=236.136 CenterZ=0 NormalX=0 NormalY=0 NormalZ=1 AngleXU=0 Radius=20
  constraints (2):
    c: Coincident(g0,g-3)
    c: Diameter(g0) = 40
FEATURE [PartDesign::Pocket] Pocket026
  BaseFeature = -> Pad025
  Direction = (0,1,-2e-16)
  Length = 0
  Length2 = 5
  Profile = -> Sketch055
  ReferenceAxis = -> Sketch055 [N_Axis]
  Refine = true
  Suppressed = false
  Type = 3
  UpToFace = -> Pad025 [Face41]
FEATURE [PartDesign::Fillet] Fillet002
  Base = -> Pocket026 [Edge101,Edge65,Edge67,Edge99]
  BaseFeature = -> Pocket026
  Radius = 18
  Refine = true
  SupportTransform = false
  Suppressed = false
  UseAllEdges = false
FEATURE [PartDesign::ShapeBinder] ShapeBinder  label="HX711 Hole Binder"
  Support = -> [Pocket027]
  TraceSupport = false
FEATURE [Sketcher::SketchObject] Sketch058
  ArcFitTolerance = 1e-06
  AttachmentSupport = -> [Fillet002]
  ExternalGeometry = -> [ShapeBinder]
  FullyConstrained = true
  MakeInternals = false
  MapMode = 5
  Placement = pos=(0,-8.43396,0) rot=(0,0.707107,0.707107;3.14159rad)
  sketch-geometry (4):
    g0: LineSegment StartX=-9.6 StartY=258.195 StartZ=0 EndX=9.6 EndY=258.195 EndZ=0
    g1: LineSegment StartX=9.6 StartY=258.195 StartZ=0 EndX=9.6 EndY=277.395 EndZ=0
    g2: LineSegment StartX=9.6 StartY=277.395 StartZ=0 EndX=-9.6 EndY=277.395 EndZ=0
    g3: LineSegment StartX=-9.6 StartY=277.395 StartZ=0 EndX=-9.6 EndY=258.195 EndZ=0
  constraints (12):
    c: Coincident(g0,g1)
    c: Coincident(g1,g2)
    c: Coincident(g2,g3)
    c: Coincident(g3,g0)
    c: Horizontal(g0)
    c: Horizontal(g2)
    c: Vertical(g1)
    c: Vertical(g3)
    c: Distance(g3,g-5) = 3
    c: Distance(g0,g-3) = 3
    c: Distance(g1,g-4) = 3
    c: Distance(g2,g-6) = 3
FEATURE [PartDesign::Pad] Pad027
  BaseFeature = -> Fillet002
  Direction = (0,1,-2e-16)
  Length = 10
  Length2 = 10
  Profile = -> Sketch058
  ReferenceAxis = -> Sketch058 [N_Axis]
  Refine = true
  Suppressed = false
  Type = 3
  UpToFace = -> Fillet002 [Face14]
FEATURE [Sketcher::SketchObject] Sketch059
  ArcFitTolerance = 1e-06
  AttachmentSupport = -> [Pad027]
  ExternalGeometry = -> [ShapeBinder]
  FullyConstrained = true
  MakeInternals = false
  MapMode = 5
  Placement = pos=(0,-11.434,0) rot=(1,0,0;1.5708rad)
  sketch-geometry (4):
    g0: LineSegment StartX=-6.6 StartY=274.395 StartZ=0 EndX=-6.6 EndY=261.195 EndZ=0
    g1: LineSegment StartX=-6.6 StartY=261.195 StartZ=0 EndX=6.6 EndY=261.195 EndZ=0
    g2: LineSegment StartX=6.6 StartY=261.195 StartZ=0 EndX=6.6 EndY=274.395 EndZ=0
    g3: LineSegment StartX=6.6 StartY=274.395 StartZ=0 EndX=-6.6 EndY=274.395 EndZ=0
  constraints (10):
    c: Coincident(g0,g1)
    c: Coincident(g1,g2)
    c: Coincident(g2,g3)
    c: Coincident(g3,g0)
    c: Vertical(g0)
    c: Vertical(g2)
    c: Horizontal(g1)
    c: Horizontal(g3)
    c: Coincident(g0,g-5)
    c: Coincident(g1,g-6)
FEATURE [PartDesign::Pocket] Pocket028
  BaseFeature = -> Pad027
  Direction = (0,1,-2e-16)
  Length = 20
  Length2 = 5
  Profile = -> Sketch059
  ReferenceAxis = -> Sketch059 [N_Axis]
  Refine = true
  Suppressed = false
  Type = 0
FEATURE [PartDesign::Fillet] Fillet005
  Base = -> Pocket028 [Face48]
  BaseFeature = -> Pocket028
  Radius = 1
  Refine = true
  SupportTransform = false
  Suppressed = false
  UseAllEdges = false
FEATURE [PartDesign::Pocket] Pocket032
  BaseFeature = -> Fillet005
  Direction = (0,0,-1)
  Length = 2
  Length2 = 5
  Profile = -> Fillet005 [Face4]
  Refine = true
  Suppressed = false
  Type = 0
FEATURE [PartDesign::Body] Body009  label="Food Plate"
  AllowCompound = false
  Group = -> [ShapeBinder,CopyPocket017,Sketch048,Pad024,Sketch050,Sketch052,Pocket025,Thickness002,Pad025,Sketch055,Pocket026,Fillet002,Sketch058,Pad027,Sketch059,Pocket028,Fillet005,Pocket032]
  Origin = -> Origin009
  Tip = -> Pocket032
COMPONENT P4 — recipe-attached ("Body010_CutLink", modeled in this document).
Construction recipe (the document's own serialized feature program — sketch geometry with constraints, then the solid features built on it; lengths are millimeters unless a unit is written):

FEATURE [PartDesign::ShapeBinder] ShapeBinder002  label="Inside Base Shape"
  Support = -> [Pocket008]
  TraceSupport = false
FEATURE [PartDesign::ShapeBinder] ShapeBinder003  label="Outside Shape"
  Support = -> [Pocket008]
  TraceSupport = false
FEATURE [PartDesign::Pad] Pad028
  Direction = (0,0,1)
  Length = 4
  Length2 = 10
  Profile = -> ShapeBinder002
  Refine = true
  Suppressed = false
  Type = 0
FEATURE [PartDesign::Pad] Pad029
  BaseFeature = -> Pad028
  Direction = (0,0,1)
  Length = 5
  Length2 = 10
  Profile = -> ShapeBinder003
  Refine = true
  Reversed = true
  Suppressed = false
  Type = 0
FEATURE [Sketcher::SketchObject] Sketch061
  ArcFitTolerance = 1e-06
  AttachmentSupport = -> [Pad029]
  ExternalGeometry = -> [Pad029]
  FullyConstrained = true
  MakeInternals = false
  MapMode = 5
  Placement = pos=(0,0,95) rot=(1,0,0;3.14159rad)
  sketch-geometry (1):
    g0: Circle CenterX=0 CenterY=-27.6169 CenterZ=0 NormalX=0 NormalY=0 NormalZ=1 AngleXU=0 Radius=12.5
  constraints (2):
    c: Diameter(g0) = 25
    c: Symmetric(g-3,g-3,g0)
FEATURE [PartDesign::Pocket] Pocket031
  BaseFeature = -> Pad029
  Direction = (0,0,1)
  Length = 5
  Length2 = 5
  Profile = -> Sketch061
  ReferenceAxis = -> Sketch061 [N_Axis]
  Refine = true
  Suppressed = false
  Type = 1
FEATURE [PartDesign::Fillet] Fillet003
  Base = -> Pocket031 [Edge49,Edge45]
  BaseFeature = -> Pocket031
  Radius = 2
  Refine = true
  SupportTransform = false
  Suppressed = false
  UseAllEdges = false
FEATURE [PartDesign::Fillet] Fillet006
  Base = -> Fillet003 [Face23]
  BaseFeature = -> Fillet003
  Radius = 1
  Refine = true
  SupportTransform = false
  Suppressed = false
  UseAllEdges = false
FEATURE [PartDesign::Thickness] Thickness003
  Base = -> Fillet006 [Face28]
  BaseFeature = -> Fillet006
  Intersection = true
  Join = 0
  Mode = 0
  Refine = true
  Reversed = true
  SupportTransform = false
  Suppressed = false
  Value = 2.6
FEATURE [PartDesign::Body] Body010  label="Storage Cover"
  AllowCompound = false
  Group = -> [ShapeBinder002,ShapeBinder003,Pad028,Pad029,Sketch061,Pocket031,Fillet003,Fillet006,Thickness003]
  Origin = -> Origin010
  Tip = -> Thickness003
COMPONENT P5 — recipe-attached ("Body_CutLink", modeled in this document).
Construction recipe (the document's own serialized feature program — sketch geometry with constraints, then the solid features built on it; lengths are millimeters unless a unit is written):

FEATURE [Sketcher::SketchObject] Sketch
  ArcFitTolerance = 1e-06
  AttachmentSupport = -> [XY_Plane]
  FullyConstrained = true
  MakeInternals = false
  MapMode = 5
  sketch-geometry (4):
    g0: LineSegment StartX=-85 StartY=-72.3831 StartZ=0 EndX=85 EndY=-72.3831 EndZ=0
    g1: LineSegment StartX=85 StartY=-72.3831 StartZ=0 EndX=85 EndY=27.6169 EndZ=0
    g2: LineSegment StartX=85 StartY=27.6169 StartZ=0 EndX=-85 EndY=27.6169 EndZ=0
    g3: LineSegment StartX=-85 StartY=27.6169 StartZ=0 EndX=-85 EndY=-72.3831 EndZ=0
  constraints (11):
    c: Coincident(g0,g1)
    c: Coincident(g1,g2)
    c: Coincident(g2,g3)
    c: Coincident(g3,g0)
    c: Horizontal(g0)
    c: Vertical(g1)
    c: Vertical(g3)
    c: Distance(g1,g3) = 170
    c: Distance(g0,g2) = 100
    c: Symmetric(g2,g1,g-2)
    c: Block(g2)
FEATURE [PartDesign::Pad] Pad  label="Base"
  Direction = (0,0,1)
  Length = 200
  Length2 = 10
  Profile = -> Sketch
  ReferenceAxis = -> Sketch [N_Axis]
  Refine = true
  Suppressed = false
  Type = 0
FEATURE [PartDesign::Fillet] Fillet  label="Round Base Corner"
  Base = -> Pad [Edge1,Edge8,Edge2,Edge5]
  BaseFeature = -> Pad
  Radius = 30
  Refine = true
  SupportTransform = false
  Suppressed = false
  UseAllEdges = false
FEATURE [PartDesign::Thickness] Thickness
  Base = -> Fillet [Face2]
  BaseFeature = -> Fillet
  Intersection = false
  Join = 0
  Mode = 0
  Refine = true
  Reversed = true
  SupportTransform = false
  Suppressed = false
  Value = 3
FEATURE [Sketcher::SketchObject] Sketch001
  ArcFitTolerance = 1e-06
  AttachmentSupport = -> [Thickness]
  ExternalGeometry = -> [Thickness]
  FullyConstrained = true
  MakeInternals = false
  MapMode = 5
  Placement = pos=(0,0,200) rot=(0,0,1;0rad)
  sketch-geometry (7):
    g0: ArcOfCircle CenterX=0 CenterY=0 CenterZ=0 NormalX=0 NormalY=0 NormalZ=1 AngleXU=0 Radius=21.5 StartAngle=5.54716 EndAngle=10.1608
    g1: Circle CenterX=0 CenterY=0 CenterZ=0 NormalX=0 NormalY=0 NormalZ=1 AngleXU=0 Radius=20
    g2: LineSegment StartX=15.9346 StartY=-14.434 StartZ=0 EndX=15.5 EndY=-14.9137 EndZ=0
    g3: LineSegment StartX=-15.9344 StartY=-14.4341 StartZ=0 EndX=-15.5 EndY=-14.9137 EndZ=0
    g4: LineSegment StartX=-15.5 StartY=-14.9137 StartZ=0 EndX=-15.5 EndY=-39.9137 EndZ=0
    g5: LineSegment StartX=15.5 StartY=-14.9137 StartZ=0 EndX=15.5 EndY=-39.9137 EndZ=0
    g6: LineSegment StartX=-15.5 StartY=-39.9137 StartZ=0 EndX=15.5 EndY=-39.9137 EndZ=0
  constraints (16):
    c: Block(g1)
    c: Block(g0)
    c: Tangent(g0,g3) = -1.5708
    c: Tangent(g0,g2) = 1.5708
    c: Distance(g4) = 25
    c: Vertical(g4)
    c: Coincident(g4,g3)
    c: Vertical(g5)
    c: Coincident(g5,g2)
    c: Coincident(g6,g4)
    c: Coincident(g6,g5)
    c: Horizontal(g6)
    c: Diameter(g1) = 40
    c: Radius(g0) = 21.5
    c: DistanceY(g5,g5) = 25
    c: DistanceX(g6,g6) = 31
FEATURE [PartDesign::Pad] Pad001  label="DoorWay"
  BaseFeature = -> Thickness
  Direction = (0,0,1)
  Length = 15
  Length2 = 10
  Profile = -> Sketch001
  ReferenceAxis = -> Sketch001 [N_Axis]
  Refine = true
  Suppressed = false
  Type = 0
FEATURE [Sketcher::SketchObject] Sketch003
  ArcFitTolerance = 1e-06
  AttachmentSupport = -> [Pad001]
  ExternalGeometry = -> [Pad001]
  FullyConstrained = true
  MakeInternals = false
  MapMode = 5
  Placement = pos=(-15.5,0,0) rot=(0.57735,-0.57735,-0.57735;2.0944rad)
  sketch-geometry (3):
    g0: ArcOfCircle CenterX=27.4137 CenterY=215 CenterZ=0 NormalX=0 NormalY=0 NormalZ=1 AngleXU=0 Radius=12.5 StartAngle=-4.35e-14 EndAngle=3.14159
    g1: LineSegment StartX=14.9137 StartY=215 StartZ=0 EndX=27.4137 EndY=215 EndZ=0
    g2: LineSegment StartX=39.9137 StartY=215 StartZ=0 EndX=27.4137 EndY=215 EndZ=0
  constraints (9):
    c: Coincident(g0,g-3)
    c: Coincident(g0,g-3)
    c: PointOnObject(g0,g-3)
    c: PointOnObject(g1,g0)
    c: Coincident(g1,g0)
    c: Horizontal(g1)
    c: PointOnObject(g2,g0)
    c: Coincident(g2,g0)
    c: Horizontal(g2)
FEATURE [PartDesign::Pad] Pad002  label="Door Hinge Form"
  BaseFeature = -> Pad001
  Direction = (-1,0,0)
  Length = 25
  Length2 = 10
  Profile = -> Sketch003
  ReferenceAxis = -> Sketch003 [N_Axis]
  Refine = true
  Suppressed = false
  Type = 3
  UpToFace = -> Pad001 [Face23]
FEATURE [PartDesign::Pocket] Pocket  label="Pocket Container"
  BaseFeature = -> Pad002
  Direction = (0,0,-1)
  Length = 5
  Length2 = 5
  Midplane = true
  Profile = -> Pad002 [Face28]
  Refine = true
  Suppressed = false
  Type = 1
FEATURE [Sketcher::SketchObject] Sketch004
  ArcFitTolerance = 1e-06
  AttachmentSupport = -> [Pocket]
  ExternalGeometry = -> [Pocket]
  FullyConstrained = true
  MakeInternals = false
  MapMode = 5
  Placement = pos=(15.5,0,0) rot=(0.57735,0.57735,0.57735;2.0944rad)
  sketch-geometry (1):
    g0: Circle CenterX=-27.4137 CenterY=215 CenterZ=0 NormalX=0 NormalY=0 NormalZ=1 AngleXU=0 Radius=4.25
  constraints (2):
    c: Diameter(g0) = 8.5
    c: Coincident(g0,g-3)
FEATURE [PartDesign::Pocket] Pocket001  label="Pocket Hinge Circle"
  BaseFeature = -> Pocket
  Direction = (-1,0,0)
  Length = 5
  Length2 = 5
  Profile = -> Sketch004 [Edge1]
  ReferenceAxis = -> Sketch004 [N_Axis]
  Refine = true
  Suppressed = false
  Type = 1
FEATURE [Sketcher::SketchObject] Sketch009
  ArcFitTolerance = 1e-06
  AttachmentSupport = -> [YZ_Plane]
  ExternalGeometry = -> [Pocket001]
  FullyConstrained = true
  MakeInternals = false
  MapMode = 5
  Placement = pos=(0,0,0) rot=(0.57735,0.57735,0.57735;2.0944rad)
  sketch-geometry (1):
    g0: Circle CenterX=-27.4137 CenterY=215 CenterZ=0 NormalX=0 NormalY=0 NormalZ=1 AngleXU=0 Radius=12.5
  constraints (3):
    c: DistanceX(g-4,g-5) = 25
    c: Coincident(g0,g-3)
    c: PointOnObject(g-5,g0)
FEATURE [PartDesign::Pocket] Pocket004  label="Pocket Doorway form"
  BaseFeature = -> Pocket001
  Direction = (-1,0,0)
  Length = 26
  Length2 = 5
  Midplane = true
  Profile = -> Sketch009
  ReferenceAxis = -> Sketch009 [N_Axis]
  Refine = true
  Suppressed = false
  Type = 0
FEATURE [PartDesign::Line] DatumLine  label="Hinge center"
  AttacherType = Attacher::AttachEngineLine
  AttachmentSupport = -> [Pocket004]
  Length = 20
  MapMode = 42
  Placement = pos=(0,-27.4425,215) rot=(0.57735,0.57735,0.57735;2.0944rad)
  ResizeMode = 0
FEATURE [PartDesign::Plane] DatumPlane  label="Door floor plane"
  AttachmentSupport = -> [DatumLine]
  Length = 62.6838
  MapMode = 3
  Placement = pos=(0,-27.4425,215) rot=(0.707107,0.707107,0;3.14159rad)
  ResizeMode = 0
  Width = 60.2413
FEATURE [PartDesign::Plane] DatumPlane001  label="Door center plane"
  AttachmentSupport = -> [DatumLine]
  Length = 74.8801
  MapMode = 2
  Placement = pos=(0,-27.4425,215) rot=(0.57735,0.57735,0.57735;2.0944rad)
  ResizeMode = 0
  Width = 262.438
FEATURE [Sketcher::SketchObject] Sketch020
  ArcFitTolerance = 1e-06
  AttachmentSupport = -> [Pocket004]
  ExternalGeometry = -> [Pocket004,DatumLine]
  FullyConstrained = true
  MakeInternals = false
  MapMode = 5
  Placement = pos=(0,0,200) rot=(0,0,1;0rad)
  sketch-geometry (9):
    g0: LineSegment StartX=-30 StartY=-27.4425 StartZ=0 EndX=-30 EndY=-6.14248 EndZ=0
    g1: LineSegment StartX=-30 StartY=-6.14248 StartZ=0 EndX=-32.5 EndY=-6.14248 EndZ=0
    g2: LineSegment StartX=-32.5 StartY=-6.14248 StartZ=0 EndX=-32.5 EndY=-11.0425 EndZ=0
    g3: LineSegment StartX=-32.5 StartY=-11.0425 StartZ=0 EndX=-48.3 EndY=-11.0425 EndZ=0
    g4: LineSegment StartX=-48.3 StartY=-11.0425 StartZ=0 EndX=-48.3 EndY=-33.6425 EndZ=0
    g5: LineSegment StartX=-48.3 StartY=-33.6425 StartZ=0 EndX=-32.5 EndY=-33.6425 EndZ=0
    g6: LineSegment StartX=-32.5 StartY=-33.6425 StartZ=0 EndX=-32.5 EndY=-38.5425 EndZ=0
    g7: LineSegment StartX=-30 StartY=-27.4425 StartZ=0 EndX=-30 EndY=-38.5425 EndZ=0
    g8: LineSegment StartX=-30 StartY=-38.5425 StartZ=0 EndX=-32.5 EndY=-38.5425 EndZ=0
  constraints (27):
    c: Vertical(g0)
    c: Vertical(g2)
    c: Horizontal(g3)
    c: Vertical(g4)
    c: Horizontal(g5)
    c: Vertical(g6)
    c: DistanceY(g2,g2) = 4.9
    c: DistanceY(g4,g4) = 22.6
    c: DistanceX(g5,g5) = 15.8
    c: DistanceX(g3,g3) = 15.8
    c: Coincident(g2,g3)
    c: Coincident(g0,g1)
    c: Coincident(g4,g5)
    c: Coincident(g3,g4)
    c: Coincident(g1,g2)
    c: Coincident(g6,g5)
    c: Horizontal(g1)
    c: DistanceX(g1,g1) = 2.5
    c: DistanceY(g6,g6) = 4.9
    c: Vertical(g7)
    c: Coincident(g7,g0)
    c: Coincident(g8,g7)
    c: Coincident(g8,g6)
    c: Horizontal(g8)
    c: DistanceY(g7,g7) = 11.1
    c: DistanceX(g7,g-9) = 14.5
    c: PointOnObject(g0,g-11)
FEATURE [PartDesign::Pad] Pad007  label="Servo seat"
  BaseFeature = -> Pocket004
  Direction = (0,0,1)
  Length = 8.8
  Length2 = 10
  Profile = -> Sketch020
  ReferenceAxis = -> Sketch020 [N_Axis]
  Refine = true
  Suppressed = false
  Type = 0
FEATURE [Sketcher::SketchObject] Sketch021
  ArcFitTolerance = 1e-06
  AttachmentSupport = -> [Pad007]
  ExternalGeometry = -> [Pad007,DatumLine]
  FullyConstrained = true
  MakeInternals = false
  MapMode = 5
  Placement = pos=(-32.5,0,0) rot=(0.57735,-0.57735,-0.57735;2.0944rad)
  sketch-geometry (14):
    g0: LineSegment StartX=38.5425 StartY=208.8 StartZ=0 EndX=38.5425 EndY=223 EndZ=0
    g1: LineSegment StartX=32.8474 StartY=223 StartZ=0 EndX=38.5425 EndY=223 EndZ=0
    g2: LineSegment StartX=38.5425 StartY=208.8 StartZ=0 EndX=38.5425 EndY=200 EndZ=0
    g3: LineSegment StartX=34.1425 StartY=208.69 StartZ=0 EndX=34.1425 EndY=221.1 EndZ=0
    g4: ArcOfCircle CenterX=33.4677 CenterY=222.032 CenterZ=0 NormalX=0 NormalY=0 NormalZ=1 AngleXU=0 Radius=1.15 StartAngle=2.14047 EndAngle=5.33948
    g5: LineSegment StartX=34.1425 StartY=208.69 StartZ=0 EndX=33.6425 EndY=200 EndZ=0
    g6: LineSegment StartX=33.6425 StartY=200 StartZ=0 EndX=38.5425 EndY=200 EndZ=0
    g7: LineSegment StartX=6.14248 StartY=208.8 StartZ=0 EndX=6.14248 EndY=223 EndZ=0
    g8: LineSegment StartX=11.8313 StartY=223 StartZ=0 EndX=6.14248 EndY=223 EndZ=0
    g9: LineSegment StartX=6.14248 StartY=208.8 StartZ=0 EndX=6.14248 EndY=200 EndZ=0
    g10: LineSegment StartX=10.5425 StartY=208.69 StartZ=0 EndX=10.5425 EndY=221.1 EndZ=0
    g11: ArcOfCircle CenterX=11.1278 CenterY=222.09 CenterZ=0 NormalX=0 NormalY=0 NormalZ=1 AngleXU=0 Radius=1.15 StartAngle=4.1784 EndAngle=7.19567
    g12: LineSegment StartX=10.5425 StartY=208.69 StartZ=0 EndX=11.0425 EndY=200 EndZ=0
    g13: LineSegment StartX=11.0425 StartY=200 StartZ=0 EndX=6.14248 EndY=200 EndZ=0
  constraints (36):
    c: Distance(g0) = 14.2
    c: Coincident(g0,g-3)
    c: Vertical(g0)
    c: Coincident(g1,g0)
    c: Coincident(g2,g0)
    c: Vertical(g3)
    c: Coincident(g4,g1)
    c: Coincident(g4,g3)
    c: Horizontal(g1,g0)
    c: Distance(g4,g3) = 1.15
    c: Angle(g4) = 3.19901
    c: Coincident(g5,g-5)
    c: Block(g5)
    c: Coincident(g3,g5)
    c: Coincident(g6,g5)
    c: Coincident(g6,g2)
    c: Horizontal(g6)
    c: DistanceX(g6,g6) = 4.9
    c: DistanceY(g3,g3) = 12.41
    c: Coincident(g8,g7)
    c: Coincident(g9,g7)
    c: Coincident(g11,g8)
    c: Block(g12)
    c: Coincident(g10,g12)
    c: Coincident(g13,g12)
    c: Coincident(g13,g9)
    c: Coincident(g-7,g9)
    c: Horizontal(g13)
    c: Vertical(g7)
    c: Vertical(g10)
    c: Horizontal(g8)
    c: DistanceY(g10,g10) = 12.41
    c: DistanceY(g7,g7) = 14.2
    c: DistanceX(g13,g13) = 4.9
    c: Coincident(g7,g-6)
    c: Block(g11)
FEATURE [PartDesign::Pad] Pad008  label="ServoHolder"
  BaseFeature = -> Pad007
  Direction = (-1,0,0)
  Length = 5
  Length2 = 10
  Profile = -> Sketch021
  ReferenceAxis = -> Sketch021 [N_Axis]
  Refine = true
  Suppressed = false
  Type = 0
FEATURE [PartDesign::LinearPattern] LinearPattern  label="Clip repeat"
  BaseFeature = -> Pad008
  Direction = -> Pad008 [Face21]
  Length = 10.82
  Mode = 0
  Occurrences = 2
  Offset = 10.82
  Originals = -> [Pad008]
  Refine = true
  Reversed = true
  Suppressed = false
  TransformMode = 0
FEATURE [PartDesign::Plane] DatumPlane002  label="Floor storage"
  AttachmentSupport = -> [LinearPattern]
  Length = 60
  MapMode = 5
  Placement = pos=(0,0,200) rot=(0,0,1;0rad)
  ResizeMode = 0
  Width = 60
FEATURE [PartDesign::SubShapeBinder] Binder004
  BindCopyOnChange = 0
  BindMode = 0
  ClaimChildren = false
  Context = -> Body [Binder004.]
  Fuse = false
  MakeFace = true
  OffsetFill = false
  OffsetIntersection = false
  OffsetJoinType = 0
  OffsetOpenResult = false
  PartialLoad = false
  Refine = true
  Relative = true
  Support = -> [LinearPattern[Face2]]
  _Version = 2
FEATURE [PartDesign::Pocket] Pocket008
  BaseFeature = -> LinearPattern
  Direction = (0,0,1)
  Length = 100
  Length2 = 5
  Profile = -> Binder004
  Refine = true
  Suppressed = false
  Type = 0
FEATURE [Sketcher::SketchObject] Sketch062
  ArcFitTolerance = 1e-06
  AttachmentSupport = -> [Pocket008]
  ExternalGeometry = -> [Pocket008]
  FullyConstrained = true
  MakeInternals = false
  MapMode = 5
  Placement = pos=(0,0,200) rot=(0,0,1;0rad)
  sketch-geometry (4):
    g0: Circle CenterX=65.69 CenterY=16.9662 CenterZ=0 NormalX=0 NormalY=0 NormalZ=1 AngleXU=0 Radius=4.25
    g1: Circle CenterX=65.69 CenterY=-59.4338 CenterZ=0 NormalX=0 NormalY=0 NormalZ=1 AngleXU=0 Radius=4.25
    g2: Circle CenterX=-67.31 CenterY=-59.4338 CenterZ=0 NormalX=0 NormalY=0 NormalZ=1 AngleXU=0 Radius=4.25
    g3: Circle CenterX=-67.31 CenterY=16.9662 CenterZ=0 NormalX=0 NormalY=0 NormalZ=1 AngleXU=0 Radius=4.25
  constraints (12):
    c: Diameter(g0) = 8.5
    c: Diameter(g1) = 8.5
    c: Diameter(g2) = 8.5
    c: Diameter(g3) = 8.5
    c: Horizontal(g1,g2)
    c: Vertical(g0,g1)
    c: Vertical(g3,g2)
    c: DistanceX(g3,g0) = 133
    c: Distance(g2,g-3) = 4.72
    c: DistanceY(g2,g3) = 76.4
    c: DistanceX(g1,g-8) = 19.31
    c: Horizontal(g3,g0)
FEATURE [PartDesign::Pocket] Pocket033
  BaseFeature = -> Pocket008
  Direction = (0,0,-1)
  Length = 5
  Length2 = 5
  Profile = -> Sketch062
  ReferenceAxis = -> Sketch062 [N_Axis]
  Refine = true
  Suppressed = false
  Type = 1
FEATURE [PartDesign::Fillet] Fillet008
  Base = -> Pocket033 [Edge120,Edge87,Edge130,Edge98]
  BaseFeature = -> Pocket033
  Radius = 1
  Refine = true
  SupportTransform = false
  Suppressed = false
  UseAllEdges = false
FEATURE [PartDesign::Body] Body  label="Food storage"
  AllowCompound = false
  Group = -> [Sketch,Pad,Fillet,Thickness,Sketch001,Pad001,Sketch003,Pad002,Pocket,Sketch004,Pocket001,Sketch009,Pocket004,DatumLine,DatumPlane,DatumPlane001,Sketch020,Pad007,Sketch021,Pad008,LinearPattern,DatumPlane002,Binder004,Pocket008,Sketch062,Pocket033,Fillet008]
  Origin = -> Origin
  Tip = -> Fillet008
PROVENANCE & LICENSES
A FreeCAD (.FCStd) document from a public repository crawl; recipes are the document's own serialized feature recipes (and, for linked parts, companion documents' recipes).
License: unknown-license-file.
